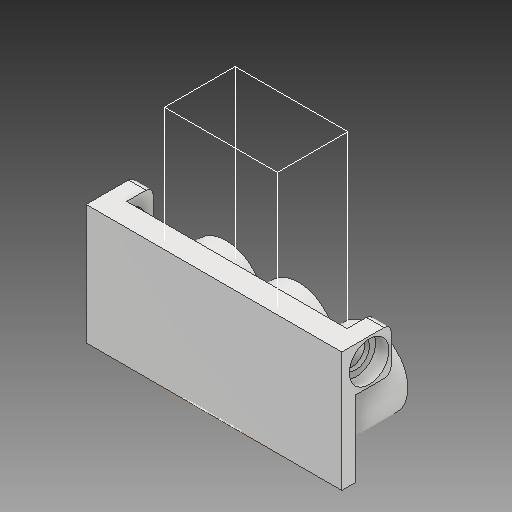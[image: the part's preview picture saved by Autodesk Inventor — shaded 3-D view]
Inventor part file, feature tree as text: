
AUTODESK INVENTOR PART (.ipt)
format: ipt  version: 2018 (Build 220112000, 112)  size: 992,256 bytes
history: native  units: mm
features: sketch x46, extrude x39, fillet x4
ambient origin geometry x8: Origin, YZ Plane, XZ Plane, XY Plane, X Axis, Y Axis, Z Axis, Center Point
bodies: Solid1 (feature_tree)
feature tree (89):
  extrude  "Extrusion1"  Depth=80.0mm
  extrude  "Extrusion2"  Depth=12.0mm
  sketch  "Sketch3"  dims[d5=12.0mm d6=14.5mm]
  extrude  "Extrusion3"  Depth=14.5mm
  extrude  "Extrusion4"  Depth=2.0mm
  extrude  "Extrusion5"  Depth=0.5mm TaperAngle=0.0deg
  sketch  "Sketch7"  dims[d15=10.0mm d16=25.0mm]
  extrude  "Extrusion6"  Depth=25.0mm
  extrude  "Extrusion7"  Depth=25.0mm
  extrude  "Extrusion8"  Depth=10.0mm
  fillet  "Fillet1"  Radius=10.0mm
  fillet  "Fillet2"  Radius=10.0mm
  extrude  "Extrusion9"  Depth=7.5mm TaperAngle=0.0deg
  extrude  "Extrusion10"  Depth=4.0mm
  fillet  "Fillet3"  Radius=3.0mm
  extrude  "Extrusion11"  Depth=21.0mm
  extrude  "Extrusion12"  Depth=41.0mm
  extrude  "Extrusion13"  Depth=42.0mm
  extrude  "Extrusion14"  Depth=38.0mm
  extrude  "Extrusion15"  Depth=45.0mm TaperAngle=0.0deg
  extrude  "Extrusion16"  Depth=3.0mm TaperAngle=0.0deg
  extrude  "Extrusion17"  Depth=3.0mm
  extrude  "Extrusion18"  Depth=39.5mm
  extrude  "Extrusion19"  Depth=7.25mm
  extrude  "Extrusion20"  Depth=125.0mm
  extrude  "Extrusion21"  Depth=10.0mm
  sketch  "Sketch24"  dims[d65=66.0mm d66=3.5mm d67=0.0mm]
  extrude  "Extrusion22"  Depth=10.0mm TaperAngle=0.0deg
  extrude  "Extrusion23"  Depth=12.0mm
  extrude  "Extrusion24"  Depth=3.5mm TaperAngle=0.0deg
  extrude  "Extrusion25"  Depth=2.0mm
  extrude  "Extrusion26"  Depth=2.0mm TaperAngle=0.0deg
  sketch  "Sketch30"  dims[d81=4.0mm d82=4.0mm]
  extrude  "Extrusion27"  Depth=16.0mm
  extrude  "Extrusion28"  Depth=2.0mm
  extrude  "Extrusion29"  Depth=2.0mm TaperAngle=0.0deg
  sketch  "Sketch34"  dims[d91=5.0mm d92=16.0mm d93=5.0mm]
  extrude  "Extrusion30"  Depth=4.0mm
  extrude  "Extrusion31"  Depth=2.0mm TaperAngle=0.0deg
  extrude  "Extrusion32"  Depth=150.0mm TaperAngle=0.0deg
  sketch  "Sketch38"  dims[d102=5.0mm d103=0.0mm d104=500.0mm d105=0.0mm]
  extrude  "Extrusion33"  Depth=16.0mm
  sketch  "Sketch40"  dims[d110=38.75mm]
  extrude  "Extrusion34"  Depth=16.0mm
  fillet  "Fillet4"  Radius=5.0mm
  extrude  "Extrusion35"  Depth=3.0mm
  extrude  "Extrusion36"  Depth=43.0mm TaperAngle=0.0deg
  extrude  "Extrusion37"  Depth=38.75mm
  extrude  "Extrusion38"  Depth=5.0mm TaperAngle=0.0deg
  extrude  "Extrusion39"  Depth=45.0mm TaperAngle=0.0deg
  sketch  "Sketch1"  dims[d0=145.0mm d1=80.0mm]
  sketch  "Sketch2"  dims[d2=3.0mm d3=0.0mm d4=12.0mm]
  sketch  "Sketch4"  dims[d7=2.0mm d8=2.0mm]
  sketch  "Sketch5"  dims[d9=6.0mm d10=0.0mm d11=0.5mm d12=0.0mm]
  sketch  "Sketch6"  dims[d13=10.0mm d14=25.0mm]
  sketch  "Sketch8"  dims[d17=25.0mm d18=0.0mm d19=22.5mm d20=10.0mm d21=0.0mm d22=10.0mm]
  sketch  "Sketch9"  dims[d23=2.5mm d24=0.0mm d25=7.5mm d26=0.0mm]
  sketch  "Sketch10"  dims[d27=10.0mm d28=0.0mm d29=4.0mm d30=3.0mm]
  sketch  "Sketch11"  dims[d31=1.0mm d32=21.0mm]
  sketch  "Sketch12"  dims[d33=38.0mm d34=41.0mm]
  sketch  "Sketch13"  dims[d35=38.0mm d36=42.0mm]
  sketch  "Sketch14"  dims[d37=41.0mm d38=38.0mm]
  sketch  "Sketch15"  dims[d39=42.0mm d40=45.0mm d41=0.0mm]
  sketch  "Sketch16"  dims[d42=12.5mm d43=3.0mm d44=0.0mm]
  sketch  "Sketch17"  dims[d45=3.0mm d46=39.5mm]
  sketch  "Sketch18"  dims[d47=39.5mm d48=39.5mm]
  sketch  "Sketch19"  dims[d49=45.0mm d50=0.0mm d51=7.25mm]
  sketch  "Sketch20"  dims[d52=4.0mm d53=7.75mm d54=0.0mm d55=0.0mm d56=125.0mm]
  sketch  "Sketch21"  dims[d57=10.0mm d58=0.0mm d59=1.0mm]
  sketch  "Sketch22"  dims[d60=14.5mm d61=10.0mm d62=0.0mm]
  sketch  "Sketch23"  dims[d63=16.0mm d64=12.0mm]
  sketch  "Sketch25"  dims[d68=4.0mm d69=2.0mm]
  sketch  "Sketch26"  dims[d70=4.0mm d71=2.0mm d72=0.0mm]
  sketch  "Sketch27"  dims[d73=2.0mm d74=0.0mm d75=16.0mm]
  sketch  "Sketch28"  dims[d76=2.0mm d77=2.0mm]
  sketch  "Sketch29"  dims[d78=2.0mm d79=3.5mm d80=0.0mm]
  sketch  "Sketch31"  dims[d83=4.0mm d84=2.0mm d85=0.0mm]
  sketch  "Sketch32"  dims[d86=15.5mm d87=150.0mm d88=0.0mm]
  sketch  "Sketch33"  dims[d89=12.0mm d90=16.0mm]
  sketch  "Sketch35"  dims[d94=12.0mm d95=3.0mm]
  sketch  "Sketch36"  dims[d96=43.0mm d97=0.0mm d98=43.0mm d99=0.0mm]
  sketch  "Sketch37"  dims[d100=38.75mm d101=38.75mm]
  sketch  "Sketch39"  dims[d106=45.0mm d107=0.0mm d108=45.0mm d109=0.0mm]
  sketch  "Sketch41"  dims[d111=38.75mm]
  sketch  "Sketch42"  dims[d112=45.0mm d113=0.0mm]
  sketch  "Sketch43"  dims[d114=3.5mm d115=0.0mm]
  sketch  "Sketch44"  dims[d116=43.0mm d117=0.0mm]
  sketch  "Sketch45"  dims[d118=100.0mm d119=0.0mm]
  sketch  "Sketch46"  dims[d120=200.0mm d121=0.0mm d122=1.5mm d123=0.0mm d124=5.0mm d125=10.0mm d126=10.0mm d127=6.35mm d128=7.0mm d129=0.0mm d130=2.75mm d131=7.0mm d132=0.0mm d133=7.75mm d134=16.0mm d135=5.0mm d136=0.0mm d137=7.0mm d138=7.0mm d139=15.0mm d140=0.0mm d141=13.5mm d142=2.0mm d143=0.0mm d144=16.0mm d145=5.0mm d146=0.0mm d147=2.0mm d148=0.0mm]
